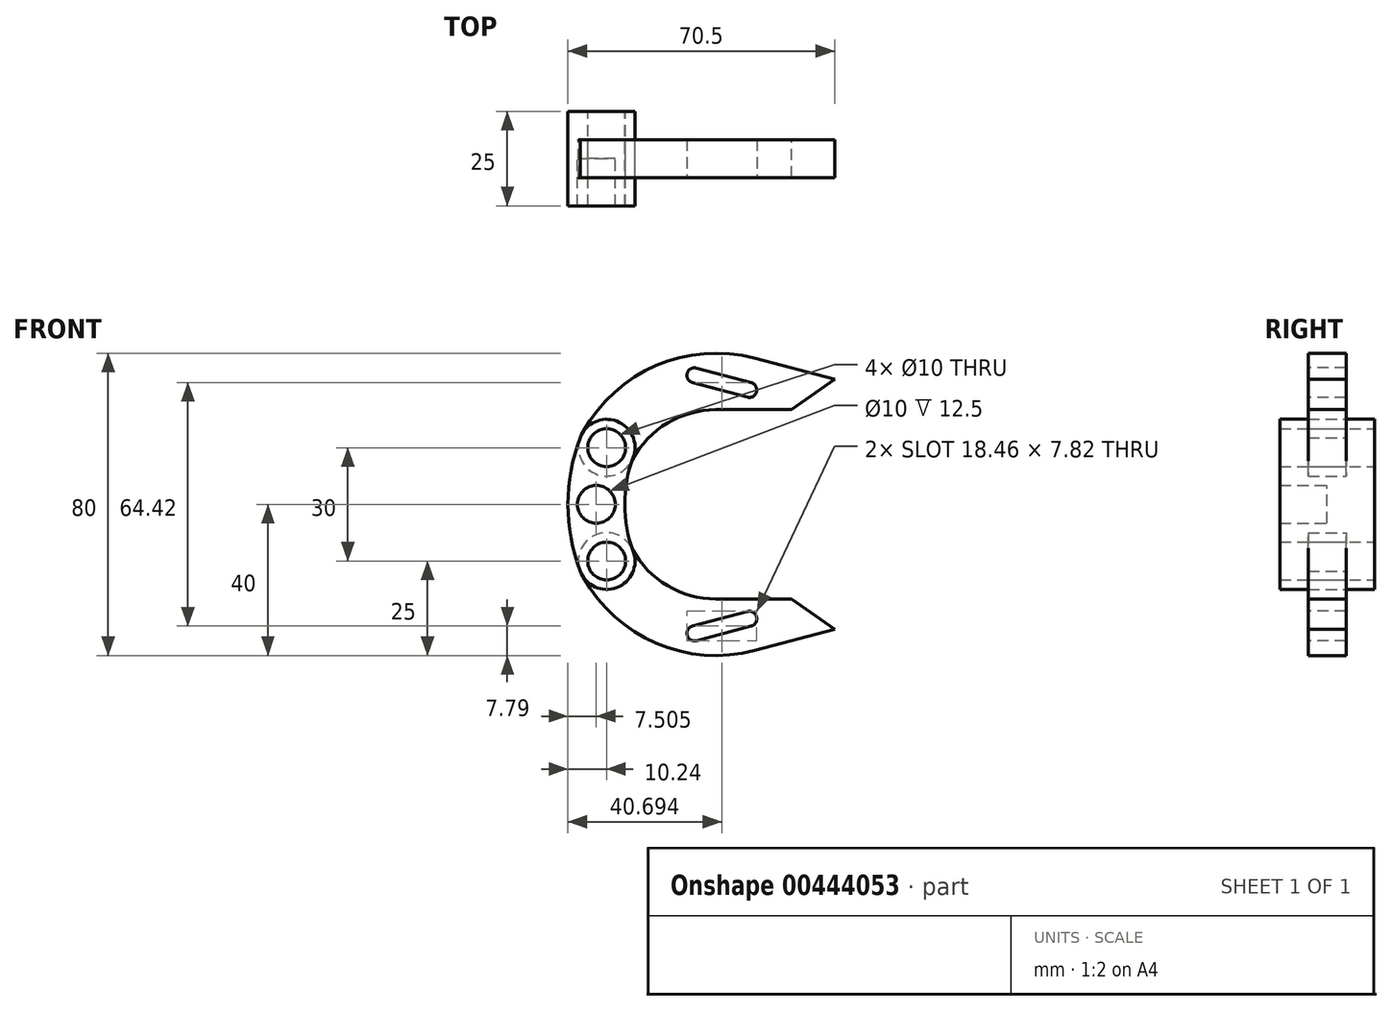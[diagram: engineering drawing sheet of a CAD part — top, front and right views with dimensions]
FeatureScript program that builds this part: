
annotation { "Feature Type Name" : "Feature", "Feature Type Description" : "" }
export const myFeature = defineFeature(function(context is Context, id is Id, definition is map)
    precondition{}
    {
        {
            var Q0;
            Q0=qCreatedBy(makeId("Front.planeOp"),FACE);
            var sketch = newSketch(context, id + "F0", { "sketchPlane" : qUnion([Q0])});
            skLineSegment(sketch, "E0", {"start": v(0, 15) * mm, "end": v(0, -15) * mm, "construction": true});
            skLineSegment(sketch, "E1", {"start": v(0, 0) * mm, "end": v(80, 0) * mm, "construction": true});
            skCircle(sketch, "E2", {"center": v(0, 15) * mm, "radius": 5 * mm});
            skCircle(sketch, "E3", {"center": v(0, -15) * mm, "radius": 5 * mm});
            skCircle(sketch, "E4.0", {"center": v(0, 15) * mm, "radius": 7.5 * mm});
            skCircle(sketch, "E5.0", {"center": v(0, -15) * mm, "radius": 7.5 * mm});
            skArc(sketch, "E6", {"start": v(-7.02, 17.65) * mm, "mid": v(-10.24, 0) * mm, "end": v(-7.02, -17.65) * mm});
            skArc(sketch, "E7", {"start": v(7.02, 12.35) * mm, "mid": v(4.76, 0) * mm, "end": v(7.02, -12.35) * mm});
            skSolve(sketch);
        }
        {
            var Q0;
            Q0=qCreatedBy(makeId("Front.planeOp"),FACE);
            var sketch = newSketch(context, id + "F1", { "sketchPlane" : qUnion([Q0])});
            skCircle(sketch, "E8.0", {"center": v(0, 15) * mm, "radius": 5 * mm});
            skArc(sketch, "E9", {"start": v(39.16, 38.66) * mm, "mid": v(12.32, 36.4) * mm, "end": v(-7.02, 17.65) * mm});
            skLineSegment(sketch, "E10", {"start": v(39.16, 38.66) * mm, "end": v(60.26, 33.04) * mm});
            skLineSegment(sketch, "E11", {"start": v(60.26, 33.04) * mm, "end": v(48.88, 25.04) * mm});
            skLineSegment(sketch, "E12", {"start": v(48.88, 25.04) * mm, "end": v(28.88, 25.04) * mm});
            skArc(sketch, "E13", {"start": v(28.88, 25.04) * mm, "mid": v(15.88, 21.4) * mm, "end": v(6.66, 11.54) * mm});
            skLineSegment(sketch, "E14", {"start": v(39.16, 38.66) * mm, "end": v(37.7, 30.28) * mm, "construction": true});
            skLineSegment(sketch, "E15", {"start": v(37.7, 30.28) * mm, "end": v(23.2, 34.14) * mm, "construction": true});
            skArc(sketch, "E16", {"start": v(23.72, 36.07) * mm, "mid": v(21.22, 34.4) * mm, "end": v(23.2, 32.14) * mm});
            skArc(sketch, "E17", {"start": v(37.7, 28.28) * mm, "mid": v(39.7, 30.1) * mm, "end": v(38.05, 32.25) * mm});
            skLineSegment(sketch, "E18", {"start": v(23.72, 36.07) * mm, "end": v(38.05, 32.26) * mm});
            skLineSegment(sketch, "E19", {"start": v(23.2, 32.14) * mm, "end": v(37.7, 28.28) * mm});
            skArc(sketch, "E20.MirrorCS", {"start": v(37.7, -28.28) * mm, "mid": v(39.7, -30.1) * mm, "end": v(38.05, -32.25) * mm});
            skArc(sketch, "E21.MirrorCS", {"start": v(23.72, -36.07) * mm, "mid": v(21.22, -34.4) * mm, "end": v(23.2, -32.14) * mm});
            skLineSegment(sketch, "E22.MirrorCS", {"start": v(23.2, -32.14) * mm, "end": v(37.7, -28.28) * mm});
            skLineSegment(sketch, "E23.MirrorCS", {"start": v(23.72, -36.07) * mm, "end": v(38.05, -32.26) * mm});
            skArc(sketch, "E24.MirrorCS", {"start": v(39.16, -38.66) * mm, "mid": v(12.32, -36.4) * mm, "end": v(-7.02, -17.65) * mm});
            skLineSegment(sketch, "E25.MirrorCS", {"start": v(39.16, -38.66) * mm, "end": v(60.26, -33.04) * mm});
            skLineSegment(sketch, "E26.MirrorCS", {"start": v(48.88, -25.04) * mm, "end": v(28.88, -25.04) * mm});
            skLineSegment(sketch, "E27.MirrorCS", {"start": v(60.26, -33.04) * mm, "end": v(48.88, -25.04) * mm});
            skArc(sketch, "E28.MirrorCS", {"start": v(28.88, -25.04) * mm, "mid": v(15.88, -21.4) * mm, "end": v(6.66, -11.54) * mm});
            skLineSegment(sketch, "E29.0", {"start": v(0, 15) * mm, "end": v(0, -15) * mm, "construction": true});
            skLineSegment(sketch, "E29.1", {"start": v(0, 0) * mm, "end": v(80, 0) * mm});
            skCircle(sketch, "E29.3", {"center": v(0, -15) * mm, "radius": 5 * mm});
            skArc(sketch, "E29.4", {"start": v(-6.2, 19.22) * mm, "mid": v(-3.46, 8.34) * mm, "end": v(7.02, 12.35) * mm});
            skArc(sketch, "E29.5", {"start": v(7.02, -12.35) * mm, "mid": v(-3.46, -8.34) * mm, "end": v(-6.2, -19.22) * mm});
            skSolve(sketch);
        }
        {
            var Q0;
            {var subQ0=sQuery(id+"F0.wireOp",EDGE,"E6");Q0=makeQuery(id+"F0.imprint","IMPRINT",FACE,{"disambiguationData":[TD([[makeQuery(id+"F0.imprint","IMPRINT",EDGE,{"derivedFrom":subQ0}),1.0]])]});}
            var Q1;
            Q1=makeQuery(id+"F0.imprint","IMPRINT",FACE,{"disambiguationData":[TD([[makeQuery(id+"F0.imprint","IMPRINT",EDGE,{"derivedFrom":sQuery(id+"F0.wireOp",EDGE,"E2")}),-1.0]])]});
            var Q2;
            Q2=makeQuery(id+"F0.imprint","IMPRINT",FACE,{"disambiguationData":[TD([[makeQuery(id+"F0.imprint","IMPRINT",EDGE,{"derivedFrom":sQuery(id+"F0.wireOp",EDGE,"E3")}),-1.0]])]});
            extrude(context, id + "F2", {"entities" : qUnion([Q0, Q1, Q2]), "endBound" : BoundingType.SYMMETRIC, "depth" : 25 * mm});
        }
        {
            var Q0;
            {var subQ8=sQuery(id+"F1.wireOp",EDGE,"E10");Q0=makeQuery(id+"F1.imprint","IMPRINT",FACE,{"disambiguationData":[TD([[makeQuery(id+"F1.imprint","IMPRINT",EDGE,{"derivedFrom":subQ8}),-1.0]])]});}
            var Q1;
            {var subQ7=sQuery(id+"F1.wireOp",EDGE,"E25.MirrorCS");Q1=makeQuery(id+"F1.imprint","IMPRINT",FACE,{"disambiguationData":[TD([[makeQuery(id+"F1.imprint","IMPRINT",EDGE,{"derivedFrom":subQ7}),1.0]])]});}
            extrude(context, id + "F3", {"entities" : qUnion([Q0, Q1]), "endBound" : BoundingType.SYMMETRIC, "depth" : 10 * mm});
        }
        {
            var Q0;
            Q0=makeQuery(id+"F3.opExtrude","CAP_FACE",FACE,{"disambiguationData":[OSD([sQuery(id+"F1.wireOp",EDGE,"E9"),sQuery(id+"F1.wireOp",EDGE,"E10"),sQuery(id+"F1.wireOp",EDGE,"E11"),sQuery(id+"F1.wireOp",EDGE,"E12"),sQuery(id+"F1.wireOp",EDGE,"E13"),sQuery(id+"F1.wireOp",EDGE,"E8.0"),sQuery(id+"F1.wireOp",EDGE,"E29.4")])],"isStart":false});
            var sketch = newSketch(context, id + "F4", { "sketchPlane" : qUnion([Q0])});
            skLineSegment(sketch, "E30", {"start": v(39.16, 38.66) * mm, "end": v(37.7, 30.28) * mm, "construction": true});
            skLineSegment(sketch, "E31", {"start": v(37.7, 30.28) * mm, "end": v(23.2, 34.14) * mm, "construction": true});
            skCircle(sketch, "E32", {"center": v(23.2, 34.14) * mm, "radius": 2 * mm});
            skCircle(sketch, "E33", {"center": v(37.7, 30.28) * mm, "radius": 2 * mm});
            skLineSegment(sketch, "E34", {"start": v(23.72, 36.07) * mm, "end": v(38.22, 32.21) * mm});
            skLineSegment(sketch, "E35", {"start": v(22.7, 32.2) * mm, "end": v(37.19, 28.35) * mm});
            skCircle(sketch, "E36.MirrorC", {"center": v(23.2, -34.14) * mm, "radius": 2 * mm});
            skLineSegment(sketch, "E37.MirrorCS", {"start": v(23.72, -36.07) * mm, "end": v(38.22, -32.21) * mm});
            skLineSegment(sketch, "E38.MirrorCS", {"start": v(22.7, -32.2) * mm, "end": v(37.19, -28.35) * mm});
            skCircle(sketch, "E39.MirrorC", {"center": v(37.7, -30.28) * mm, "radius": 2 * mm});
            skLineSegment(sketch, "E40.MirrorCS", {"start": v(37.7, -30.28) * mm, "end": v(23.2, -34.14) * mm, "construction": true});
            skSolve(sketch);
        }
        {
            var Q0;
            Q0 = qSketchRegion(id + "F4", true);
            extrude(context, id + "F5", {"entities" : qUnion([Q0]), "operationType" : NewBodyOperationType.REMOVE, "endBound" : BoundingType.THROUGH_ALL, "oppositeDirection" : true, "depth" : 25 * mm});
        }
        {
            var Q0;
            Q0=qCreatedBy(makeId("Front.planeOp"),FACE);
            var sketch = newSketch(context, id + "F6", { "sketchPlane" : qUnion([Q0])});
            skArc(sketch, "E41", {"start": v(0, 15) * mm, "mid": v(-2.74, 0) * mm, "end": v(0, -15) * mm, "construction": true});
            skCircle(sketch, "E42", {"center": v(-2.74, 0) * mm, "radius": 5 * mm});
            skCircle(sketch, "E43", {"center": v(-2.74, 0) * mm, "radius": 6 * mm, "construction": true});
            skSolve(sketch);
        }
        {
            var Q0;
            Q0 = qSketchRegion(id + "F6", true);
            var Q1;
            Q1=sQuery(id+"F6.wireOp",EDGE,"E42");
            extrude(context, id + "F7", {"entities" : qUnion([Q0]), "operationType" : NewBodyOperationType.REMOVE, "surfaceEntities" : qUnion([Q1]), "endBound" : BoundingType.THROUGH_ALL, "depth" : 25 * mm});
        }
    });
